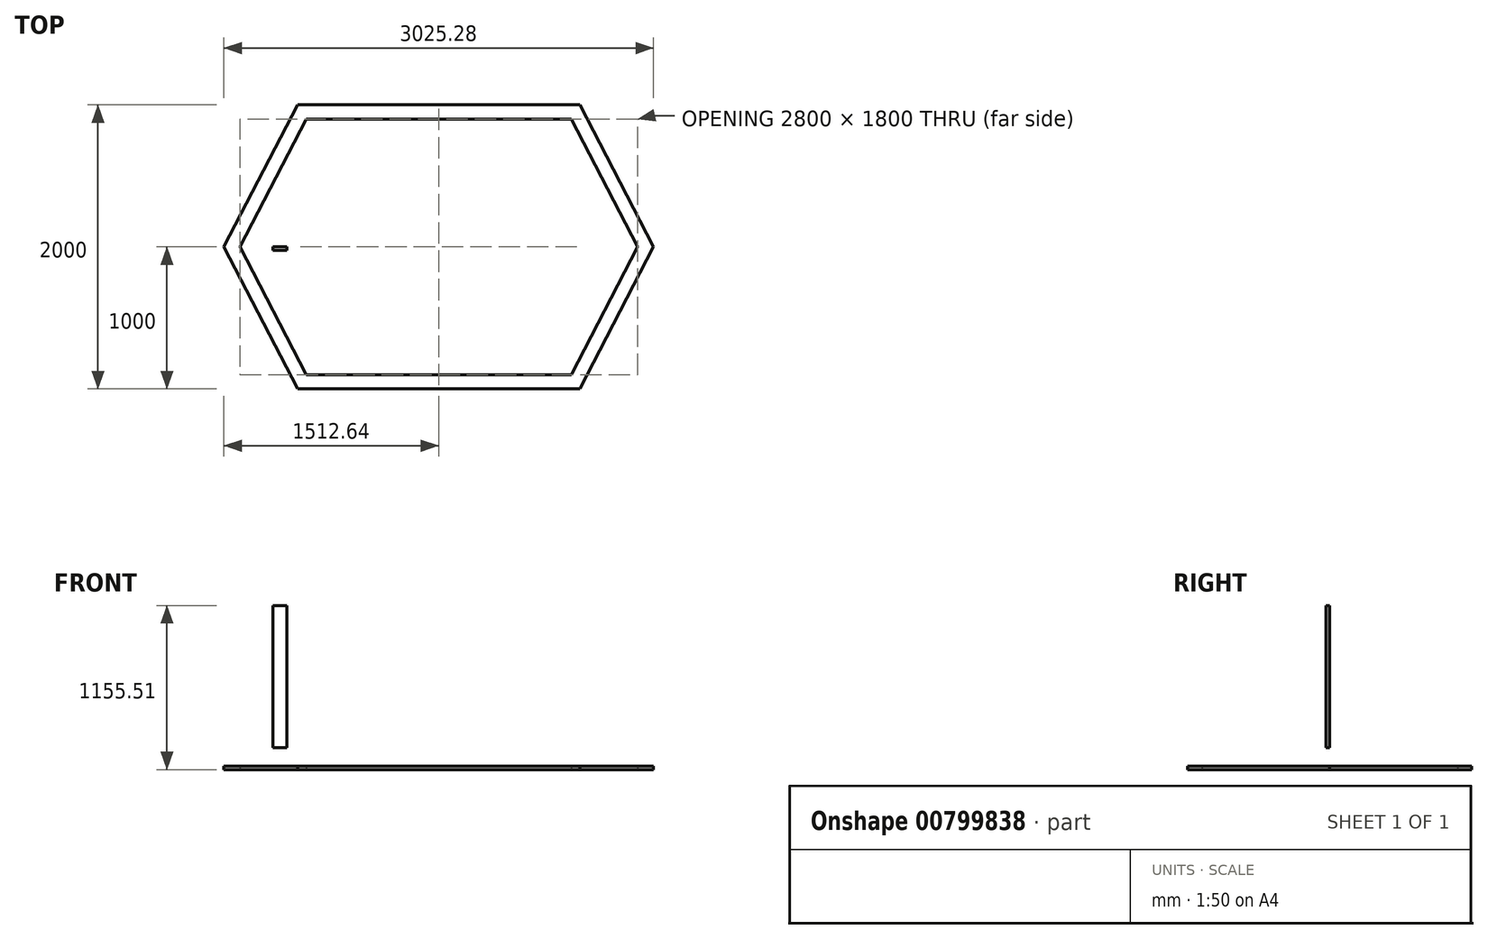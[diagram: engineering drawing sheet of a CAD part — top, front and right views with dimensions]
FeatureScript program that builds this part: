
annotation { "Feature Type Name" : "Feature", "Feature Type Description" : "" }
export const myFeature = defineFeature(function(context is Context, id is Id, definition is map)
    precondition{}
    {
        {
            var Q0;
            Q0=qCreatedBy(makeId("Top.planeOp"),FACE);
            var sketch = newSketch(context, id + "F0", { "sketchPlane" : qUnion([Q0])});
            skEllipticalArc(sketch, "E0", {});
            skLineSegment(sketch, "E1", {"start": v(-1400, 0) * mm, "end": v(1400, 0) * mm});
            skLineSegment(sketch, "E2", {"start": v(0, 900) * mm, "end": v(0, -900) * mm});
            skLineSegment(sketch, "E3.0", {"start": v(1400, 0) * mm, "end": v(933.33, -900) * mm});
            skLineSegment(sketch, "E3.1", {"start": v(933.33, -900) * mm, "end": v(-933.33, -900) * mm});
            skLineSegment(sketch, "E3.2", {"start": v(-933.33, -900) * mm, "end": v(-1400, 0) * mm});
            skLineSegment(sketch, "E3.3", {"start": v(-1400, 0) * mm, "end": v(-933.33, 900) * mm});
            skLineSegment(sketch, "E3.4", {"start": v(-933.33, 900) * mm, "end": v(933.33, 900) * mm});
            skLineSegment(sketch, "E3.5", {"start": v(933.33, 900) * mm, "end": v(1400, 0) * mm});
            skPoint(sketch, "E3.0.midPoint", {"position": v(1166.67, -450) * mm});
            skLineSegment(sketch, "E4.0", {"start": v(-1512.64, 0) * mm, "end": v(-994.13, 1000) * mm});
            skLineSegment(sketch, "E4.1", {"start": v(994.13, 1000) * mm, "end": v(1512.64, 0) * mm});
            skLineSegment(sketch, "E4.2", {"start": v(1512.64, 0) * mm, "end": v(994.13, -1000) * mm});
            skLineSegment(sketch, "E4.3", {"start": v(-994.13, 1000) * mm, "end": v(994.13, 1000) * mm});
            skLineSegment(sketch, "E4.4", {"start": v(994.13, -1000) * mm, "end": v(-994.13, -1000) * mm});
            skLineSegment(sketch, "E4.5", {"start": v(-994.13, -1000) * mm, "end": v(-1512.64, 0) * mm});
            skEllipticalArc(sketch, "E5.trimOffspring", {});
            const initialGuessF0  = {"E0": [0, 0, 1, 0, 1.25, 0.75, 3.785093762383077, 5.639684198386302], "E5.trimOffspring": [0, 0, 1, 0, 1.25, 0.75, 0.6435011087932848, 2.4980915447965093]};
            skSetInitialGuess(sketch, initialGuessF0);
            skSolve(sketch);
        }
        {
            var Q0;
            Q0 = qSketchRegion(id + "F0", true);
            extrude(context, id + "F1", {"entities" : qUnion([Q0]), "depth" : 25 * mm, "offsetDistance" : 25 * mm});
        }
        {
            var Q0;
            Q0=qCreatedBy(makeId("Front.planeOp"),FACE);
            var sketch = newSketch(context, id + "F2", { "sketchPlane" : qUnion([Q0])});
            skLineSegment(sketch, "E6.bottom", {"start": v(-1167.73, 1155.5) * mm, "end": v(-1067.73, 1155.5) * mm});
            skLineSegment(sketch, "E6.top", {"start": v(-1167.73, 155.5) * mm, "end": v(-1067.73, 155.5) * mm});
            skLineSegment(sketch, "E6.left", {"start": v(-1167.73, 1155.5) * mm, "end": v(-1167.73, 155.5) * mm});
            skLineSegment(sketch, "E6.right", {"start": v(-1067.73, 1155.5) * mm, "end": v(-1067.73, 155.5) * mm});
            skSolve(sketch);
        }
        {
            var Q0;
            Q0=makeQuery(id+"F2.imprint","IMPRINT",FACE,{"disambiguationData":[TD([[makeQuery(id+"F2.imprint","IMPRINT",EDGE,{"derivedFrom":sQuery(id+"F2.wireOp",EDGE,"E6.bottom")}),-1.0]])]});
            extrude(context, id + "F3", {"entities" : qUnion([Q0]), "depth" : 25 * mm, "offsetDistance" : 25 * mm});
        }
    });
